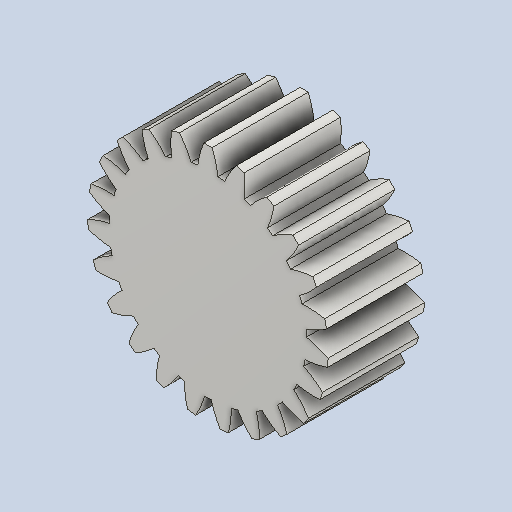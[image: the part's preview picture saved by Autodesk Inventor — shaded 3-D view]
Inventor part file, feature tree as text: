
AUTODESK INVENTOR PART (.ipt)
format: ipt  version: 2023.2 (Build 272271000, 271)  size: 271,360 bytes
history: native  units: mm (DEFAULTED — no unit token found)
features: plane x3, other x3, sketch x2, extrude x1
ambient origin geometry x8: Origin, YZ Plane, XZ Plane, XY Plane, X Axis, Y Axis, Z Axis, Center Point
bodies: Solid1 (feature_tree)
feature tree (9):
  extrude  "Extrusion1"  Depth=20.0mm TaperAngle=0.0deg
  plane  "Work Plane2"
  plane  "Work Plane8"
  plane  "Work Plane9"
  other  "Spur Gear"
  sketch  "Sketch1"  dims[d0=50.0mm d1=20.0mm d2=0.0mm]
  sketch  "Sketch2"  dims[d3=46.0mm d4=10.0mm d5=0.0mm d16=80.0mm d17=0.0mm d34=1.36591mm d39=0.0mm d41=0.0mm d43=80.0mm d46=80.0mm d47=0.0mm d48=0.0mm]
  other  "Srf1"
  other  "Pitch Diameter"
